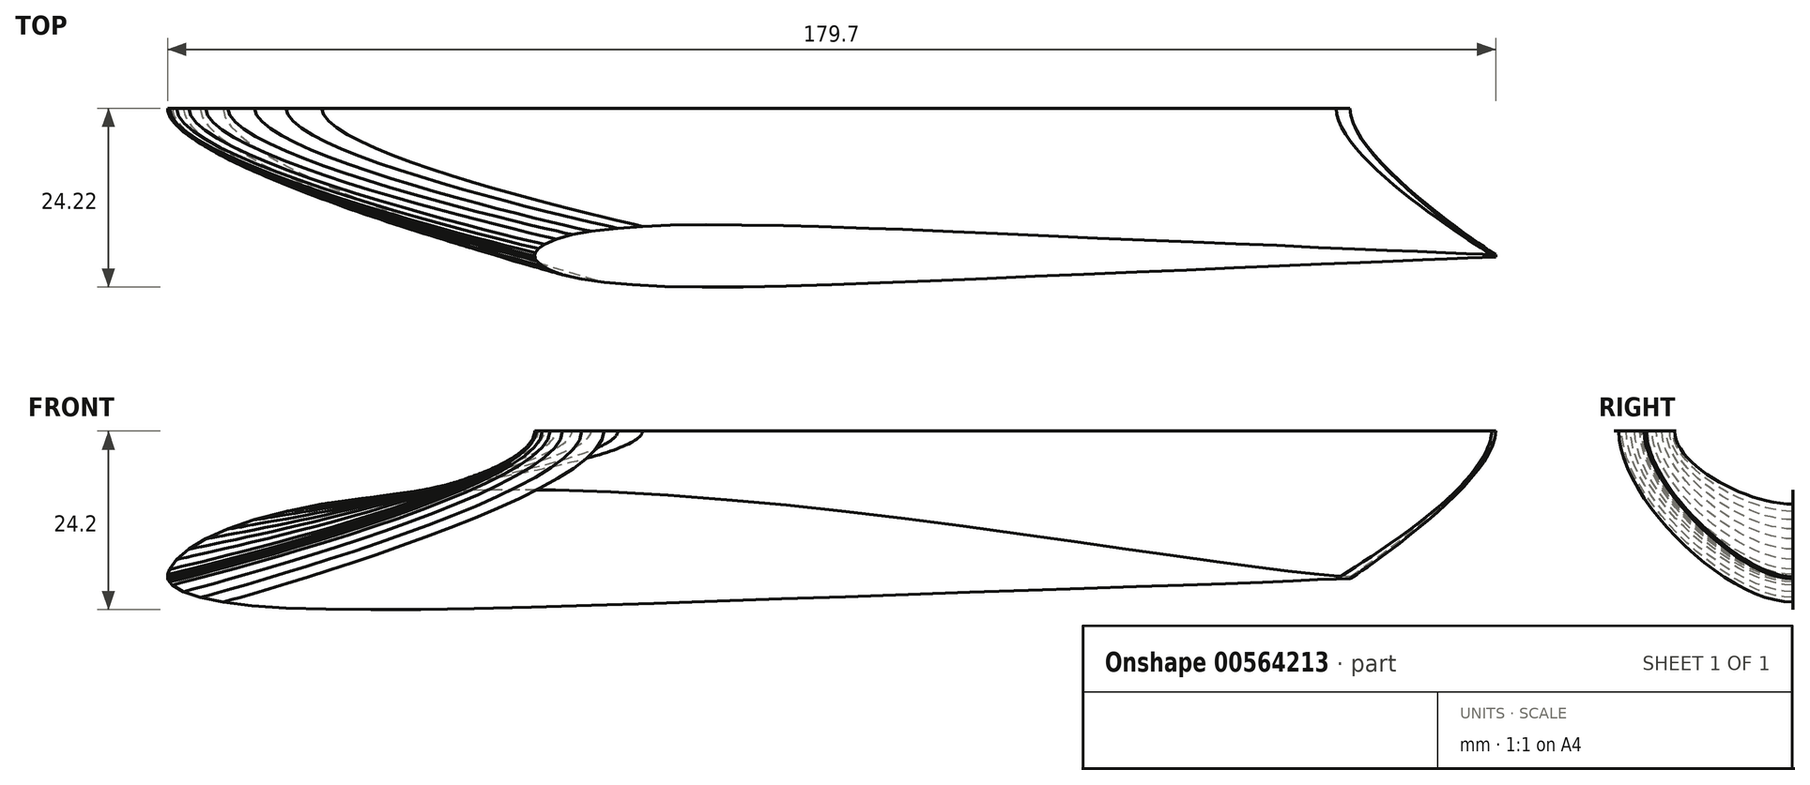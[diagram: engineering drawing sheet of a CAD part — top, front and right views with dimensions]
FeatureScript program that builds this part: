
annotation { "Feature Type Name" : "Feature", "Feature Type Description" : "" }
export const myFeature = defineFeature(function(context is Context, id is Id, definition is map)
    precondition{}
    {
        {
            var Q0;
            Q0=qCreatedBy(makeId("Top.planeOp"),FACE);
            cPlane(context, id + "F0", {"entities" : qUnion([Q0]), "cplaneType" : CPlaneType.OFFSET, "offset" : 20 * mm, "width" : 150 * mm, "height" : 150 * mm});
        }
        {
            var Q0;
            Q0=qCreatedBy(id+"F0.planeOp",FACE);
            var sketch = newSketch(context, id + "F1", { "sketchPlane" : qUnion([Q0])});
            skLineSegment(sketch, "E0", {"start": v(19.7, -19.84) * mm, "end": v(19.16, -19.85) * mm});
            skLineSegment(sketch, "E1", {"start": v(19.16, -19.85) * mm, "end": v(17.98, -19.78) * mm});
            skLineSegment(sketch, "E2", {"start": v(17.98, -19.78) * mm, "end": v(15.76, -19.7) * mm});
            skLineSegment(sketch, "E3", {"start": v(15.76, -19.7) * mm, "end": v(12.9, -19.56) * mm});
            skLineSegment(sketch, "E4", {"start": v(12.9, -19.56) * mm, "end": v(9.15, -19.4) * mm});
            skLineSegment(sketch, "E5", {"start": v(9.15, -19.4) * mm, "end": v(5.03, -19.25) * mm});
            skLineSegment(sketch, "E6", {"start": v(5.03, -19.25) * mm, "end": v(0.59, -19.04) * mm});
            skLineSegment(sketch, "E7", {"start": v(0.59, -19.04) * mm, "end": v(-4.3, -18.86) * mm});
            skLineSegment(sketch, "E8", {"start": v(-4.3, -18.86) * mm, "end": v(-9.93, -18.58) * mm});
            skLineSegment(sketch, "E9", {"start": v(-9.93, -18.58) * mm, "end": v(-15.46, -18.4) * mm});
            skLineSegment(sketch, "E10", {"start": v(-15.46, -18.4) * mm, "end": v(-21.25, -18.11) * mm});
            skLineSegment(sketch, "E11", {"start": v(-21.25, -18.11) * mm, "end": v(-27.83, -17.85) * mm});
            skLineSegment(sketch, "E12", {"start": v(-27.83, -17.85) * mm, "end": v(-34.17, -17.6) * mm});
            skLineSegment(sketch, "E13", {"start": v(-34.17, -17.6) * mm, "end": v(-40.77, -17.32) * mm});
            skLineSegment(sketch, "E14", {"start": v(-40.77, -17.32) * mm, "end": v(-47.7, -16.97) * mm});
            skLineSegment(sketch, "E15", {"start": v(-47.7, -16.97) * mm, "end": v(-53.75, -16.74) * mm});
            skLineSegment(sketch, "E16", {"start": v(-53.75, -16.74) * mm, "end": v(-60.52, -16.43) * mm});
            skLineSegment(sketch, "E17", {"start": v(-60.52, -16.43) * mm, "end": v(-65.14, -16.26) * mm});
            skLineSegment(sketch, "E18", {"start": v(-65.14, -16.26) * mm, "end": v(-71.91, -16.02) * mm});
            skLineSegment(sketch, "E19", {"start": v(-71.91, -16.02) * mm, "end": v(-76.64, -15.9) * mm});
            skLineSegment(sketch, "E20", {"start": v(-76.64, -15.9) * mm, "end": v(-82.29, -15.8) * mm});
            skLineSegment(sketch, "E21", {"start": v(-82.29, -15.8) * mm, "end": v(-87.14, -15.78) * mm});
            skLineSegment(sketch, "E22", {"start": v(-87.14, -15.78) * mm, "end": v(-92, -15.85) * mm});
            skLineSegment(sketch, "E23", {"start": v(-92, -15.85) * mm, "end": v(-95.73, -16) * mm});
            skLineSegment(sketch, "E24", {"start": v(-95.73, -16) * mm, "end": v(-99.09, -16.25) * mm});
            skLineSegment(sketch, "E25", {"start": v(-99.09, -16.25) * mm, "end": v(-102.67, -16.66) * mm});
            skLineSegment(sketch, "E26", {"start": v(-102.67, -16.66) * mm, "end": v(-105.25, -17.11) * mm});
            skLineSegment(sketch, "E27", {"start": v(-105.25, -17.11) * mm, "end": v(-107.38, -17.72) * mm});
            skLineSegment(sketch, "E28", {"start": v(-107.38, -17.72) * mm, "end": v(-108.98, -18.44) * mm});
            skLineSegment(sketch, "E29", {"start": v(-108.98, -18.44) * mm, "end": v(-109.81, -19.02) * mm});
            skLineSegment(sketch, "E30", {"start": v(-109.81, -19.02) * mm, "end": v(-110.22, -19.6) * mm});
            skLineSegment(sketch, "E31", {"start": v(-110.22, -19.6) * mm, "end": v(-110.3, -20) * mm});
            skLineSegment(sketch, "E32", {"start": v(-110.3, -20) * mm, "end": v(-110.27, -20.22) * mm});
            skLineSegment(sketch, "E33", {"start": v(-110.27, -20.22) * mm, "end": v(-110.22, -20.45) * mm});
            skLineSegment(sketch, "E34", {"start": v(-110.22, -20.45) * mm, "end": v(-110.08, -20.67) * mm});
            skLineSegment(sketch, "E35", {"start": v(-110.08, -20.67) * mm, "end": v(-109.3, -21.38) * mm});
            skLineSegment(sketch, "E36", {"start": v(-109.3, -21.38) * mm, "end": v(-108.23, -21.93) * mm});
            skLineSegment(sketch, "E37", {"start": v(-108.23, -21.93) * mm, "end": v(-106.57, -22.53) * mm});
            skLineSegment(sketch, "E38", {"start": v(-106.57, -22.53) * mm, "end": v(-103.96, -23.13) * mm});
            skLineSegment(sketch, "E39", {"start": v(-103.96, -23.13) * mm, "end": v(-100.94, -23.57) * mm});
            skLineSegment(sketch, "E40", {"start": v(-100.94, -23.57) * mm, "end": v(-97.12, -23.91) * mm});
            skLineSegment(sketch, "E41", {"start": v(-97.12, -23.91) * mm, "end": v(-92.73, -24.14) * mm});
            skLineSegment(sketch, "E42", {"start": v(-92.73, -24.14) * mm, "end": v(-87.63, -24.2) * mm});
            skLineSegment(sketch, "E43", {"start": v(-87.63, -24.2) * mm, "end": v(-82.12, -24.22) * mm});
            skLineSegment(sketch, "E44", {"start": v(-82.12, -24.22) * mm, "end": v(-76.28, -24.06) * mm});
            skLineSegment(sketch, "E45", {"start": v(-76.28, -24.06) * mm, "end": v(-70.12, -23.88) * mm});
            skLineSegment(sketch, "E46", {"start": v(-70.12, -23.88) * mm, "end": v(-63.57, -23.67) * mm});
            skLineSegment(sketch, "E47", {"start": v(-63.57, -23.67) * mm, "end": v(-56.78, -23.4) * mm});
            skLineSegment(sketch, "E48", {"start": v(-56.78, -23.4) * mm, "end": v(-49.1, -23.04) * mm});
            skLineSegment(sketch, "E49", {"start": v(-49.1, -23.04) * mm, "end": v(-42.6, -22.76) * mm});
            skLineSegment(sketch, "E50", {"start": v(-42.6, -22.76) * mm, "end": v(-36.05, -22.49) * mm});
            skLineSegment(sketch, "E51", {"start": v(-36.05, -22.49) * mm, "end": v(-28.85, -22.17) * mm});
            skLineSegment(sketch, "E52", {"start": v(-28.85, -22.17) * mm, "end": v(-22.14, -21.9) * mm});
            skLineSegment(sketch, "E53", {"start": v(-22.14, -21.9) * mm, "end": v(-15.69, -21.62) * mm});
            skLineSegment(sketch, "E54", {"start": v(-15.69, -21.62) * mm, "end": v(-9.54, -21.37) * mm});
            skLineSegment(sketch, "E55", {"start": v(-9.54, -21.37) * mm, "end": v(-3.88, -21.13) * mm});
            skLineSegment(sketch, "E56", {"start": v(-3.88, -21.13) * mm, "end": v(1.4, -20.9) * mm});
            skLineSegment(sketch, "E57", {"start": v(1.4, -20.9) * mm, "end": v(5.8, -20.72) * mm});
            skLineSegment(sketch, "E58", {"start": v(5.8, -20.72) * mm, "end": v(9.8, -20.54) * mm});
            skLineSegment(sketch, "E59", {"start": v(9.8, -20.54) * mm, "end": v(13.11, -20.43) * mm});
            skLineSegment(sketch, "E60", {"start": v(13.11, -20.43) * mm, "end": v(15.93, -20.29) * mm});
            skLineSegment(sketch, "E61", {"start": v(15.93, -20.29) * mm, "end": v(17.9, -20.2) * mm});
            skLineSegment(sketch, "E62", {"start": v(17.9, -20.2) * mm, "end": v(19.7, -20.13) * mm});
            skLineSegment(sketch, "E63", {"start": v(19.7, -20.13) * mm, "end": v(19.7, -19.84) * mm});
            skSolve(sketch);
        }
        {
            var Q0;
            Q0=qCreatedBy(makeId("Front.planeOp"),FACE);
            var sketch = newSketch(context, id + "F2", { "sketchPlane" : qUnion([Q0])});
            skLineSegment(sketch, "E64", {"start": v(0, 0.27) * mm, "end": v(-0.56, 0.3) * mm});
            skLineSegment(sketch, "E65", {"start": v(-0.56, 0.3) * mm, "end": v(-2.2, 0.4) * mm});
            skLineSegment(sketch, "E66", {"start": v(-2.2, 0.4) * mm, "end": v(-4.85, 0.64) * mm});
            skLineSegment(sketch, "E67", {"start": v(-4.85, 0.64) * mm, "end": v(-8.43, 1.04) * mm});
            skLineSegment(sketch, "E68", {"start": v(-8.43, 1.04) * mm, "end": v(-12.86, 1.6) * mm});
            skLineSegment(sketch, "E69", {"start": v(-12.86, 1.6) * mm, "end": v(-18.04, 2.29) * mm});
            skLineSegment(sketch, "E70", {"start": v(-18.04, 2.29) * mm, "end": v(-23.9, 3.1) * mm});
            skLineSegment(sketch, "E71", {"start": v(-23.9, 3.1) * mm, "end": v(-30.35, 4.03) * mm});
            skLineSegment(sketch, "E72", {"start": v(-30.35, 4.03) * mm, "end": v(-37.3, 5.02) * mm});
            skLineSegment(sketch, "E73", {"start": v(-37.3, 5.02) * mm, "end": v(-44.65, 6.06) * mm});
            skLineSegment(sketch, "E74", {"start": v(-44.65, 6.06) * mm, "end": v(-52.32, 7.1) * mm});
            skLineSegment(sketch, "E75", {"start": v(-52.32, 7.1) * mm, "end": v(-60.2, 8.12) * mm});
            skLineSegment(sketch, "E76", {"start": v(-60.2, 8.12) * mm, "end": v(-68.23, 9.09) * mm});
            skLineSegment(sketch, "E77", {"start": v(-68.23, 9.09) * mm, "end": v(-76.31, 9.96) * mm});
            skLineSegment(sketch, "E78", {"start": v(-76.31, 9.96) * mm, "end": v(-84.36, 10.71) * mm});
            skLineSegment(sketch, "E79", {"start": v(-84.36, 10.71) * mm, "end": v(-92.3, 11.32) * mm});
            skLineSegment(sketch, "E80", {"start": v(-92.3, 11.32) * mm, "end": v(-100.04, 11.75) * mm});
            skLineSegment(sketch, "E81", {"start": v(-100.04, 11.75) * mm, "end": v(-107.54, 12) * mm});
            skLineSegment(sketch, "E82", {"start": v(-107.54, 12) * mm, "end": v(-114.72, 12.04) * mm});
            skLineSegment(sketch, "E83", {"start": v(-114.72, 12.04) * mm, "end": v(-121.52, 11.88) * mm});
            skLineSegment(sketch, "E84", {"start": v(-121.52, 11.88) * mm, "end": v(-127.88, 11.5) * mm});
            skLineSegment(sketch, "E85", {"start": v(-127.88, 11.5) * mm, "end": v(-133.77, 10.9) * mm});
            skLineSegment(sketch, "E86", {"start": v(-133.77, 10.9) * mm, "end": v(-139.14, 10.1) * mm});
            skLineSegment(sketch, "E87", {"start": v(-139.14, 10.1) * mm, "end": v(-143.97, 9.12) * mm});
            skLineSegment(sketch, "E88", {"start": v(-143.97, 9.12) * mm, "end": v(-148.2, 7.98) * mm});
            skLineSegment(sketch, "E89", {"start": v(-148.2, 7.98) * mm, "end": v(-151.82, 6.73) * mm});
            skLineSegment(sketch, "E90", {"start": v(-151.82, 6.73) * mm, "end": v(-154.8, 5.38) * mm});
            skLineSegment(sketch, "E91", {"start": v(-154.8, 5.38) * mm, "end": v(-157.13, 4) * mm});
            skLineSegment(sketch, "E92", {"start": v(-157.13, 4) * mm, "end": v(-158.77, 2.6) * mm});
            skLineSegment(sketch, "E93", {"start": v(-158.77, 2.6) * mm, "end": v(-159.73, 1.27) * mm});
            skLineSegment(sketch, "E94", {"start": v(-159.73, 1.27) * mm, "end": v(-159.97, 0.57) * mm});
            skLineSegment(sketch, "E95", {"start": v(-159.97, 0.57) * mm, "end": v(-160, 0.3) * mm});
            skLineSegment(sketch, "E96", {"start": v(-160, 0.3) * mm, "end": v(-159.98, 0.04) * mm});
            skLineSegment(sketch, "E97", {"start": v(-159.98, 0.04) * mm, "end": v(-159.89, -0.2) * mm});
            skLineSegment(sketch, "E98", {"start": v(-159.89, -0.2) * mm, "end": v(-159.73, -0.44) * mm});
            skLineSegment(sketch, "E99", {"start": v(-159.73, -0.44) * mm, "end": v(-159.34, -0.86) * mm});
            skLineSegment(sketch, "E100", {"start": v(-159.34, -0.86) * mm, "end": v(-157.85, -1.76) * mm});
            skLineSegment(sketch, "E101", {"start": v(-157.85, -1.76) * mm, "end": v(-155.56, -2.55) * mm});
            skLineSegment(sketch, "E102", {"start": v(-155.56, -2.55) * mm, "end": v(-152.48, -3.18) * mm});
            skLineSegment(sketch, "E103", {"start": v(-152.48, -3.18) * mm, "end": v(-148.6, -3.65) * mm});
            skLineSegment(sketch, "E104", {"start": v(-148.6, -3.65) * mm, "end": v(-143.95, -3.96) * mm});
            skLineSegment(sketch, "E105", {"start": v(-143.95, -3.96) * mm, "end": v(-138.56, -4.14) * mm});
            skLineSegment(sketch, "E106", {"start": v(-138.56, -4.14) * mm, "end": v(-132.48, -4.2) * mm});
            skLineSegment(sketch, "E107", {"start": v(-132.48, -4.2) * mm, "end": v(-125.76, -4.16) * mm});
            skLineSegment(sketch, "E108", {"start": v(-125.76, -4.16) * mm, "end": v(-118.5, -4.04) * mm});
            skLineSegment(sketch, "E109", {"start": v(-118.5, -4.04) * mm, "end": v(-110.75, -3.85) * mm});
            skLineSegment(sketch, "E110", {"start": v(-110.75, -3.85) * mm, "end": v(-102.62, -3.61) * mm});
            skLineSegment(sketch, "E111", {"start": v(-102.62, -3.61) * mm, "end": v(-94.21, -3.34) * mm});
            skLineSegment(sketch, "E112", {"start": v(-94.21, -3.34) * mm, "end": v(-85.61, -3.05) * mm});
            skLineSegment(sketch, "E113", {"start": v(-85.61, -3.05) * mm, "end": v(-76.93, -2.74) * mm});
            skLineSegment(sketch, "E114", {"start": v(-76.93, -2.74) * mm, "end": v(-68.27, -2.44) * mm});
            skLineSegment(sketch, "E115", {"start": v(-68.27, -2.44) * mm, "end": v(-59.74, -2.14) * mm});
            skLineSegment(sketch, "E116", {"start": v(-59.74, -2.14) * mm, "end": v(-51.45, -1.85) * mm});
            skLineSegment(sketch, "E117", {"start": v(-51.45, -1.85) * mm, "end": v(-43.49, -1.58) * mm});
            skLineSegment(sketch, "E118", {"start": v(-43.49, -1.58) * mm, "end": v(-35.95, -1.32) * mm});
            skLineSegment(sketch, "E119", {"start": v(-35.95, -1.32) * mm, "end": v(-28.94, -1.08) * mm});
            skLineSegment(sketch, "E120", {"start": v(-28.94, -1.08) * mm, "end": v(-22.53, -0.87) * mm});
            skLineSegment(sketch, "E121", {"start": v(-22.53, -0.87) * mm, "end": v(-16.82, -0.67) * mm});
            skLineSegment(sketch, "E122", {"start": v(-16.82, -0.67) * mm, "end": v(-11.85, -0.48) * mm});
            skLineSegment(sketch, "E123", {"start": v(-11.85, -0.48) * mm, "end": v(-7.7, -0.3) * mm});
            skLineSegment(sketch, "E124", {"start": v(-7.7, -0.3) * mm, "end": v(-4.43, -0.13) * mm});
            skLineSegment(sketch, "E125", {"start": v(-4.43, -0.13) * mm, "end": v(-1.86, -0.02) * mm});
            skLineSegment(sketch, "E126", {"start": v(-1.86, -0.02) * mm, "end": v(0, 0) * mm});
            skLineSegment(sketch, "E127", {"start": v(0, 0) * mm, "end": v(0, 0.27) * mm});
            skSolve(sketch);
        }
        {
            var Q0;
            Q0 = qSketchRegion(id + "F2", true);
            var Q1;
            Q1 = qSketchRegion(id + "F1", true);
            loft(context, id + "F3", {"startCondition" : LoftEndDerivativeType.NORMAL_TO_PROFILE, "startMagnitude" : 1, "endCondition" : LoftEndDerivativeType.NORMAL_TO_PROFILE, "endMagnitude" : 1, "sheetProfilesArray" : [{ "sheetProfileEntities" : qUnion([Q0]) }, { "sheetProfileEntities" : qUnion([Q1]) }]});
        }
    });
